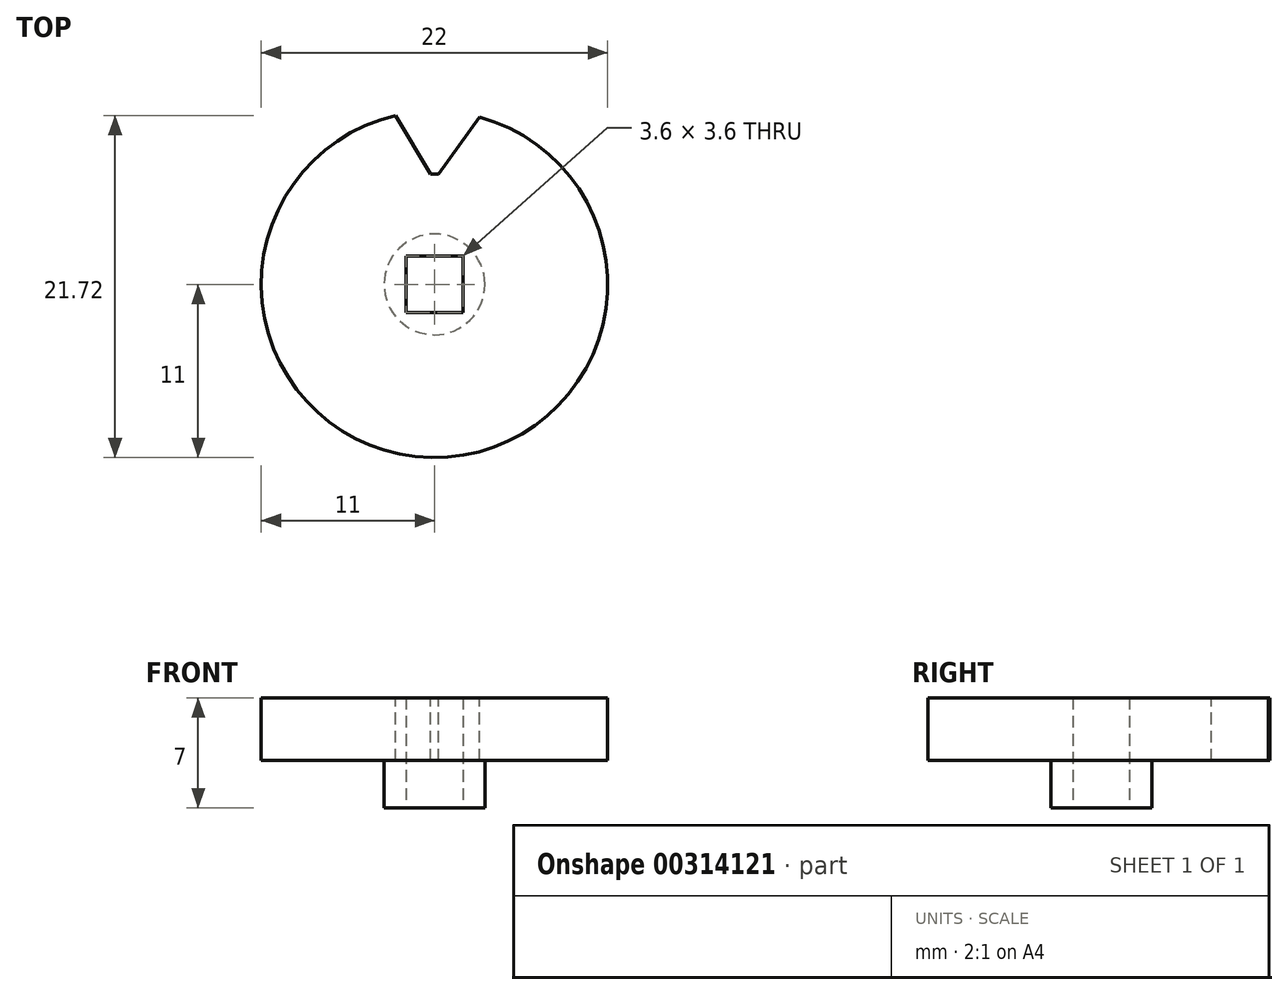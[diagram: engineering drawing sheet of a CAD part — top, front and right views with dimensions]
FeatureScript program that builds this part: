
annotation { "Feature Type Name" : "Feature", "Feature Type Description" : "" }
export const myFeature = defineFeature(function(context is Context, id is Id, definition is map)
    precondition{}
    {
        {
            var Q0;
            Q0=qCreatedBy(makeId("Top.planeOp"),FACE);
            var sketch = newSketch(context, id + "F0", { "sketchPlane" : qUnion([Q0])});
            skCircle(sketch, "E0", {"center": v(0, 0) * mm, "radius": 11 * mm});
            skSolve(sketch);
        }
        {
            var Q0;
            Q0 = qSketchRegion(id + "F0", true);
            extrude(context, id + "F1", {"entities" : qUnion([Q0]), "depth" : 4 * mm});
        }
        {
            var Q0;
            Q0=makeQuery(id+"F1.opExtrude","CAP_FACE",FACE,{"disambiguationData":[OSD([sQuery(id+"F0.wireOp",EDGE,"E0")])],"isStart":false});
            var sketch = newSketch(context, id + "F2", { "sketchPlane" : qUnion([Q0])});
            skLineSegment(sketch, "E1", {"start": v(0, 0) * mm, "end": v(0, 11) * mm});
            skLineSegment(sketch, "E2", {"start": v(0, 0) * mm, "end": v(-0.24, 7) * mm});
            skLineSegment(sketch, "E3", {"start": v(0, 0) * mm, "end": v(0.24, 7) * mm});
            skLineSegment(sketch, "E4", {"start": v(0, 0) * mm, "end": v(2.85, 10.63) * mm});
            skLineSegment(sketch, "E5", {"start": v(0, 0) * mm, "end": v(-2.47, 10.72) * mm});
            skArc(sketch, "E6", {"start": v(-0.24, 7) * mm, "mid": v(0, 7) * mm, "end": v(0.24, 7) * mm});
            skArc(sketch, "E7", {"start": v(-2.47, 10.72) * mm, "mid": v(0.2, 11) * mm, "end": v(2.85, 10.63) * mm});
            skLineSegment(sketch, "E8", {"start": v(-0.24, 7) * mm, "end": v(-2.47, 10.72) * mm});
            skLineSegment(sketch, "E9", {"start": v(0.24, 7) * mm, "end": v(2.85, 10.63) * mm});
            skSolve(sketch);
        }
        {
            var Q0;
            {var subQ5=sQuery(id+"F2.wireOp",EDGE,"E9");Q0=makeQuery(id+"F2.imprint","IMPRINT",FACE,{"disambiguationData":[TD([[makeQuery(id+"F2.imprint","IMPRINT",EDGE,{"derivedFrom":subQ5}),1.0]])]});}
            var Q1;
            {var subQ5=sQuery(id+"F2.wireOp",EDGE,"E8");Q1=makeQuery(id+"F2.imprint","IMPRINT",FACE,{"disambiguationData":[TD([[makeQuery(id+"F2.imprint","IMPRINT",EDGE,{"derivedFrom":subQ5}),-1.0]])]});}
            extrude(context, id + "F3", {"entities" : qUnion([Q0, Q1]), "operationType" : NewBodyOperationType.REMOVE, "endBound" : BoundingType.THROUGH_ALL, "oppositeDirection" : true, "depth" : 25 * mm});
        }
        {
            var Q0;
            Q0=qCreatedBy(makeId("Front.planeOp"),FACE);
            var sketch = newSketch(context, id + "F4", { "sketchPlane" : qUnion([Q0])});
            skLineSegment(sketch, "E10", {"start": v(0, 0) * mm, "end": v(0, -12.9) * mm});
            skSolve(sketch);
        }
        {
            var Q0;
            Q0=makeQuery(id+"F1.opExtrude","CAP_FACE",FACE,{"disambiguationData":[OSD([sQuery(id+"F0.wireOp",EDGE,"E0")])],"isStart":true});
            var sketch = newSketch(context, id + "F5", { "sketchPlane" : qUnion([Q0])});
            skCircle(sketch, "E11", {"center": v(0, 0) * mm, "radius": 3.2 * mm});
            skSolve(sketch);
        }
        {
            var Q0;
            Q0=makeQuery(id+"F5.imprint","IMPRINT",FACE,{"disambiguationData":[TD([[makeQuery(id+"F5.imprint","IMPRINT",EDGE,{"derivedFrom":sQuery(id+"F5.wireOp",EDGE,"E11")}),1.0]])]});
            extrude(context, id + "F6", {"entities" : qUnion([Q0]), "operationType" : NewBodyOperationType.ADD, "depth" : 3 * mm});
        }
        {
            var Q0;
            Q0=makeQuery(id+"F6.opExtrude","CAP_FACE",FACE,{"disambiguationData":[OSD([sQuery(id+"F5.wireOp",EDGE,"E11")])],"isStart":false});
            var sketch = newSketch(context, id + "F7", { "sketchPlane" : qUnion([Q0])});
            skLineSegment(sketch, "E12.bottom", {"start": v(1.8, 1.8) * mm, "end": v(-1.8, 1.8) * mm});
            skLineSegment(sketch, "E12.top", {"start": v(1.8, -1.8) * mm, "end": v(-1.8, -1.8) * mm});
            skLineSegment(sketch, "E12.left", {"start": v(1.8, 1.8) * mm, "end": v(1.8, -1.8) * mm});
            skLineSegment(sketch, "E12.right", {"start": v(-1.8, 1.8) * mm, "end": v(-1.8, -1.8) * mm});
            skPoint(sketch, "E12.middle", {"position": v(0, 0) * mm});
            skSolve(sketch);
        }
        {
            var Q0;
            Q0 = qSketchRegion(id + "F7", true);
            extrude(context, id + "F8", {"entities" : qUnion([Q0]), "operationType" : NewBodyOperationType.REMOVE, "endBound" : BoundingType.THROUGH_ALL, "oppositeDirection" : true, "depth" : 25 * mm});
        }
    });
